# Revit family: SWA-D
name_source: partatom
category: Air Terminals
revit_build: Autodesk Revit MEP 2012 (Build: 20110309_2315(x64)
units: mm (PartAtom-declared; Revit-internal decimal feet)

## types (5) — shared parameters
Ancho A = 22 5/8"
Cuello = Redondo
Diametro exterior = 5 7/8"
Diametro int = 5 7/8"
Diametro interior = 5 11/16"
Largo B = 23 5/8"
Largo parte superior = 23 5/8"
Manufacturer = INNES
Material = Acero
Medida A = 22 13/16"
Medida B = 23 13/16"
Máxima presión total = 0.00 in-wg
Máxima velocidad de cuello = 1200 FPM
Máximo flujo de aire = 0 CFM
Mínima presión total = 0.00 in-wg
Mínima velocidad de cuello = 100 FPM
Mínimo flujo de aire = 0 CFM
Radio int = 2 15/16"
URL = http://www.innes.com

## per-type parameters (varying)
| type | Diametro | Max Flow | Min Flow | Radio |
| SWA-D-06 | 6" | 236 CFM | 20 CFM | 3" |
| SWA-D-08 | 8" | 419 CFM | 35 CFM | 4" |
| SWA-D-10 | 10" | 654 CFM | 55 CFM | 5" |
| SWA-D-12 | 12" | 942 CFM | 79 CFM | 6" |
| SWA-D-14 | 14" | 1283 CFM | 107 CFM | 7" |

## geometry (parser evidence)
native form markers: Sweep x3
no freeform markers — native parametric forms only
